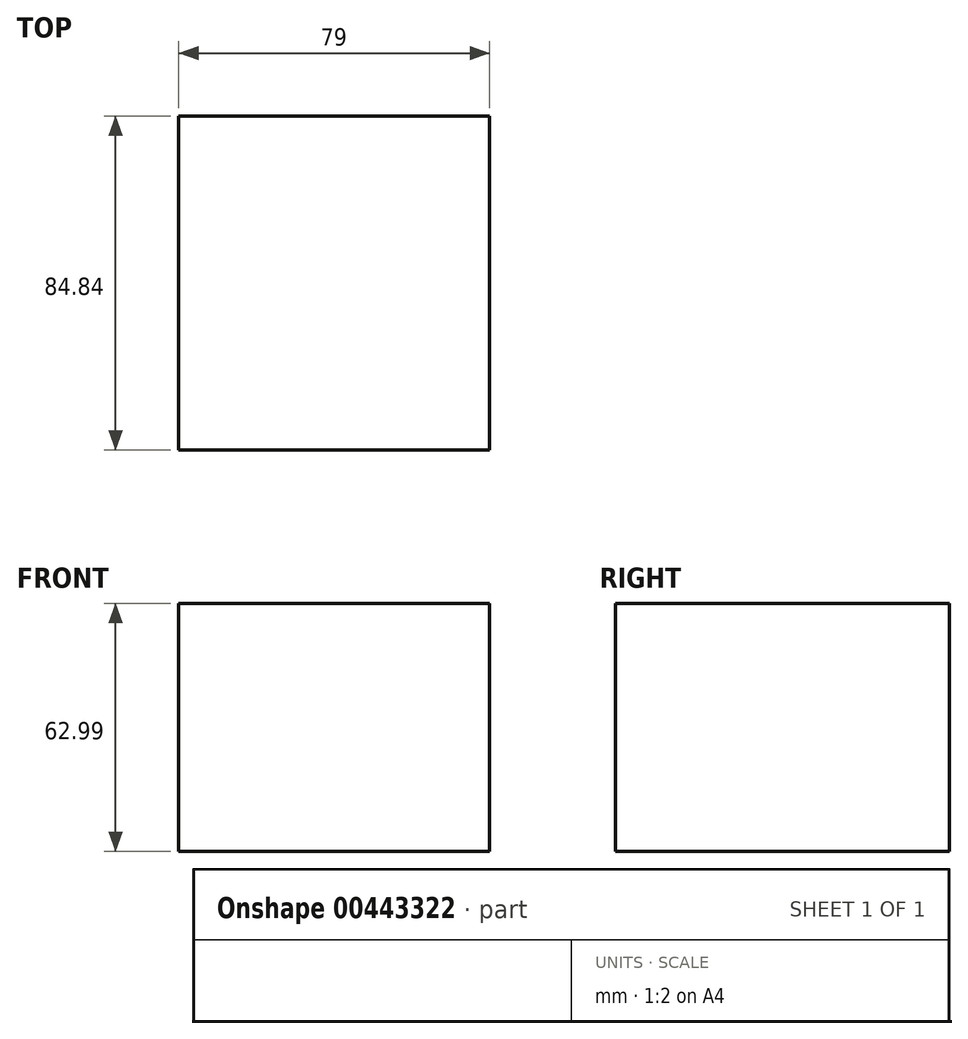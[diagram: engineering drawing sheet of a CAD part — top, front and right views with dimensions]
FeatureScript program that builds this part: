
annotation { "Feature Type Name" : "Feature", "Feature Type Description" : "" }
export const myFeature = defineFeature(function(context is Context, id is Id, definition is map)
    precondition{}
    {
        {
            var Q0;
            Q0=qCreatedBy(makeId("Top.planeOp"),FACE);
            var sketch = newSketch(context, id + "F0", { "sketchPlane" : qUnion([Q0])});
            skLineSegment(sketch, "E0.bottom", {"start": v(-39.5, 42.42) * mm, "end": v(39.5, 42.42) * mm});
            skLineSegment(sketch, "E0.top", {"start": v(-39.5, -42.42) * mm, "end": v(39.5, -42.42) * mm});
            skLineSegment(sketch, "E0.left", {"start": v(-39.5, 42.42) * mm, "end": v(-39.5, -42.42) * mm});
            skLineSegment(sketch, "E0.right", {"start": v(39.5, 42.42) * mm, "end": v(39.5, -42.42) * mm});
            skPoint(sketch, "E0.middle", {"position": v(0, 0) * mm});
            skSolve(sketch);
        }
        {
            var Q0;
            Q0=makeQuery(id+"F0.imprint","IMPRINT",FACE,{"disambiguationData":[TD([[makeQuery(id+"F0.imprint","IMPRINT",EDGE,{"derivedFrom":sQuery(id+"F0.wireOp",EDGE,"E0.bottom")}),-1.0]])]});
            extrude(context, id + "F1", {"entities" : qUnion([Q0]), "depth" : 63 * mm});
        }
    });
